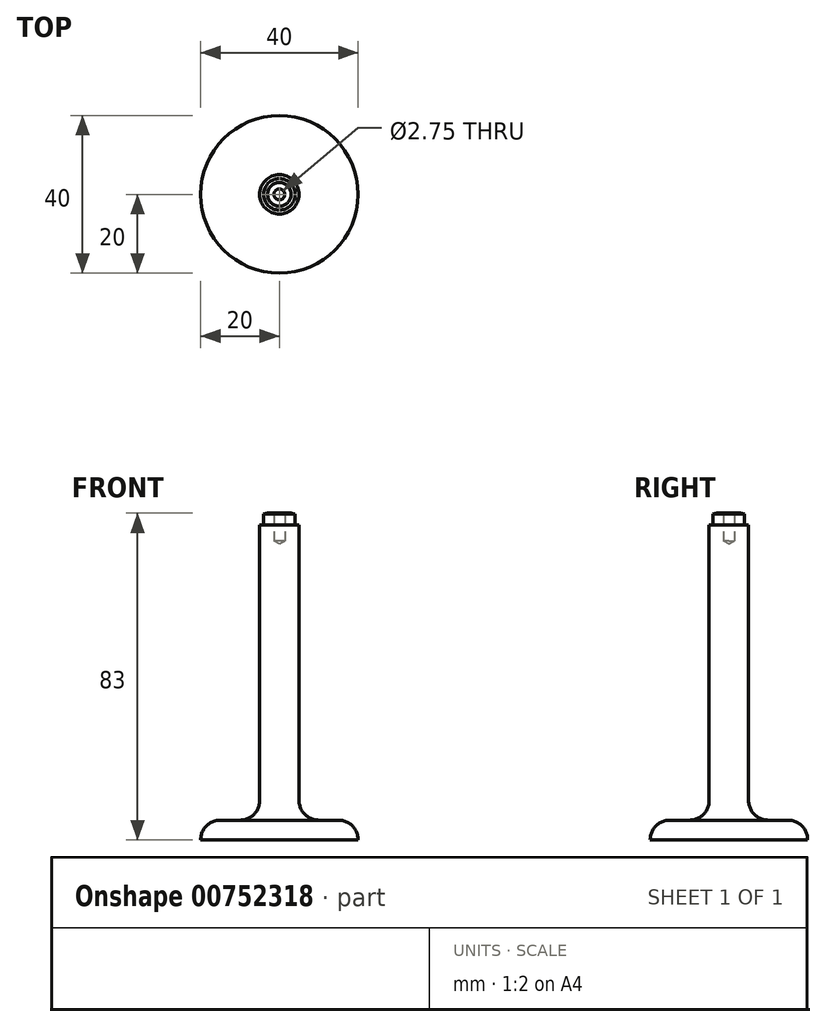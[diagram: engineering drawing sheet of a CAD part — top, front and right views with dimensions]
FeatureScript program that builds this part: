
annotation { "Feature Type Name" : "Feature", "Feature Type Description" : "" }
export const myFeature = defineFeature(function(context is Context, id is Id, definition is map)
    precondition{}
    {
        {
            var Q0;
            Q0=qCreatedBy(makeId("Top.planeOp"),FACE);
            var sketch = newSketch(context, id + "F0", { "sketchPlane" : qUnion([Q0])});
            skCircle(sketch, "E0", {"center": v(0, 0) * mm, "radius": 20 * mm});
            skSolve(sketch);
        }
        {
            var Q0;
            Q0 = qSketchRegion(id + "F0", true);
            extrude(context, id + "F1", {"entities" : qUnion([Q0]), "depth" : 5 * mm, "offsetDistance" : 25 * mm});
        }
        {
            var Q0;
            Q0=makeQuery(id+"F1.opExtrude","CAP_FACE",FACE,{"disambiguationData":[OSD([sQuery(id+"F0.wireOp",EDGE,"E0")])],"isStart":false});
            var sketch = newSketch(context, id + "F2", { "sketchPlane" : qUnion([Q0])});
            skCircle(sketch, "E1", {"center": v(0, 0) * mm, "radius": 5 * mm});
            skSolve(sketch);
        }
        {
            var Q0;
            Q0 = qSketchRegion(id + "F2", true);
            extrude(context, id + "F3", {"entities" : qUnion([Q0]), "operationType" : NewBodyOperationType.ADD, "depth" : 75 * mm, "offsetDistance" : 25 * mm});
        }
        {
            var Q0;
            Q0=makeQuery(id+"F3.opExtrude","CAP_FACE",FACE,{"disambiguationData":[OSD([sQuery(id+"F2.wireOp",EDGE,"E1")])],"isStart":false});
            var sketch = newSketch(context, id + "F4", { "sketchPlane" : qUnion([Q0])});
            skCircle(sketch, "E2", {"center": v(0, 0) * mm, "radius": 4 * mm});
            skSolve(sketch);
        }
        {
            var Q0;
            Q0 = qSketchRegion(id + "F4", true);
            extrude(context, id + "F5", {"entities" : qUnion([Q0]), "operationType" : NewBodyOperationType.ADD, "depth" : 3 * mm, "offsetDistance" : 25 * mm});
        }
        {
            var Q0;
            Q0=makeQuery(id+"F5.opExtrude","CAP_EDGE",EDGE,{"disambiguationData":[OSD([sQuery(id+"F4.wireOp",EDGE,"E2")])],"isStart":false});
            chamfer(context, id + "F6", {"entities" : qUnion([Q0]), "chamferType" : ChamferType.TWO_OFFSETS, "width1" : .25 * mm, "oppositeDirection" : false, "width2" : 1 * mm, "tangentPropagation" : true});
        }
        {
            var Q0;
            Q0=makeQuery(id+"F1.opExtrude","CAP_FACE",FACE,{"disambiguationData":[OSD([sQuery(id+"F0.wireOp",EDGE,"E0")])],"isStart":false});
            fillet(context, id + "F7", {"entities" : qUnion([Q0]), "radius" : 5 * mm, "tangentPropagation" : true, "allowEdgeOverflow" : false});
        }
        {
            var Q0;
            Q0=makeQuery(id+"F5.opExtrude","CAP_FACE",FACE,{"disambiguationData":[OSD([sQuery(id+"F4.wireOp",EDGE,"E2")])],"isStart":false});
            var sketch = newSketch(context, id + "F8", { "sketchPlane" : qUnion([Q0])});
            skPoint(sketch, "E3", {"position": v(0, 0) * mm});
            skSolve(sketch);
        }
        {
            var Q0;
            Q0=sQuery(id+"F8.wireOp",VERTEX,"E3");
            var Q1;
            Q1=makeQuery(id+"F1.opExtrude","SWEPT_BODY",BODY,{"disambiguationData":[OSD([sQuery(id+"F0.wireOp",EDGE,"E0")])]});
            hole(context, id + "F9", {"style" : HoleStyle.SIMPLE, "endStyle" : HoleEndStyle.BLIND, "holeDiameter" : 2.75 * mm, "majorDiameter" : 5 * mm, "holeDepth" : 7 * mm, "isTappedThrough" : true, "tappedDepth" : 12 * mm, "tapClearance" : 3, "locations" : qUnion([Q0]), "scope" : qUnion([Q1]), "startStyle" : HoleStartStyle.SKETCH});
        }
    });
